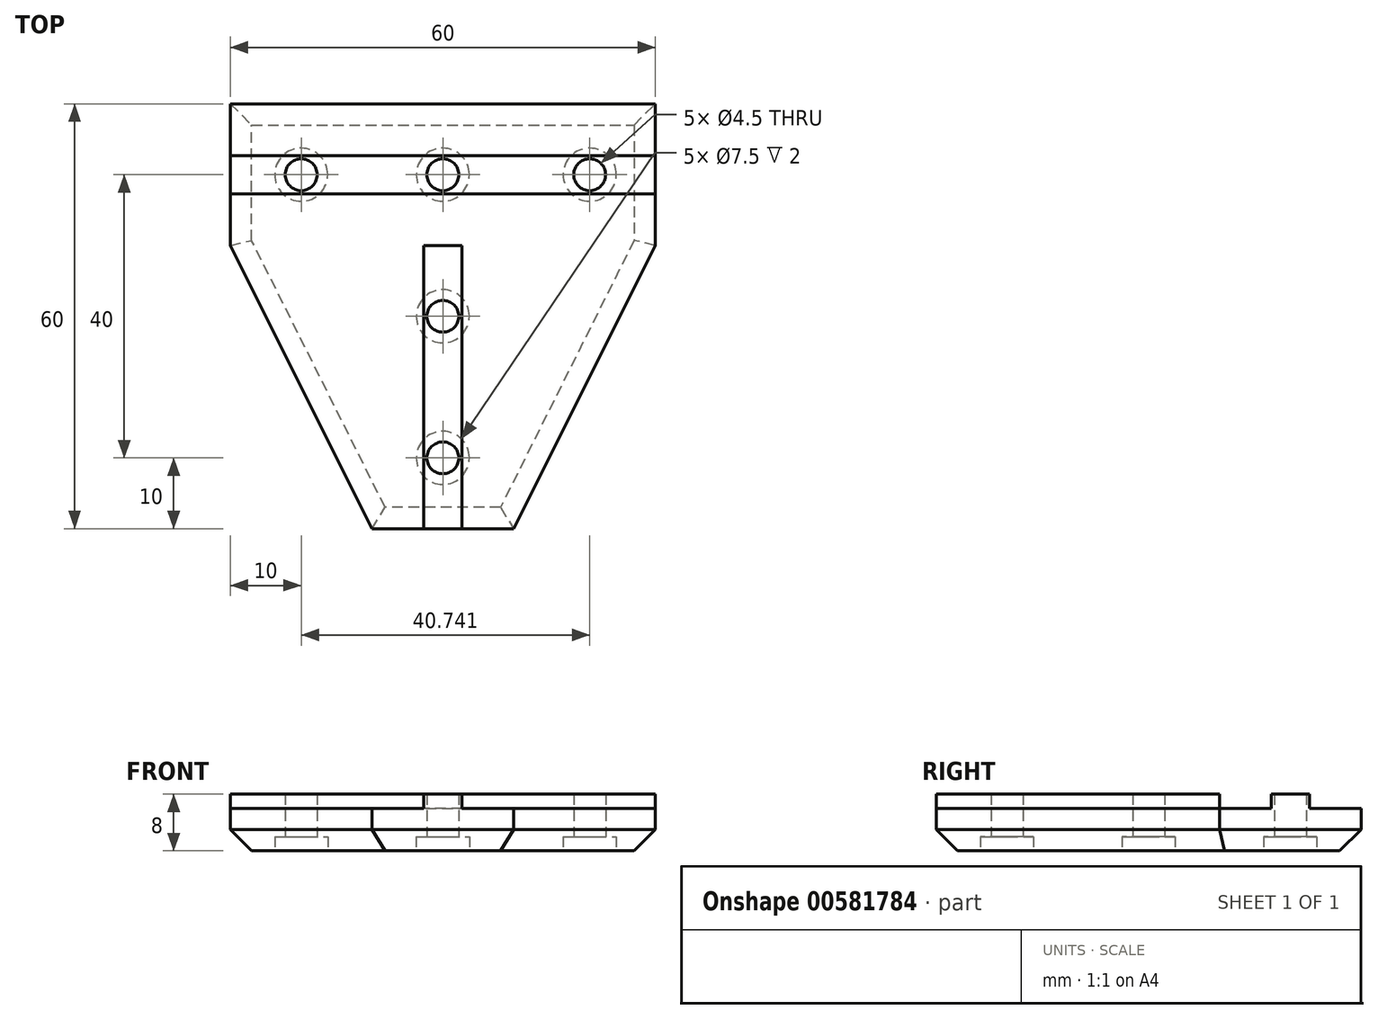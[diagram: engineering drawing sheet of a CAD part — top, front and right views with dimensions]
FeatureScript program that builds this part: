
annotation { "Feature Type Name" : "Feature", "Feature Type Description" : "" }
export const myFeature = defineFeature(function(context is Context, id is Id, definition is map)
    precondition{}
    {
        {
            var Q0;
            Q0=qCreatedBy(makeId("Top.planeOp"),FACE);
            var sketch = newSketch(context, id + "F0", { "sketchPlane" : qUnion([Q0])});
            skLineSegment(sketch, "E0", {"start": v(0, 0) * mm, "end": v(0, 20) * mm, "construction": true});
            skLineSegment(sketch, "E1", {"start": v(0, 0) * mm, "end": v(0, -40) * mm, "construction": true});
            skLineSegment(sketch, "E2", {"start": v(-10, 0) * mm, "end": v(-30, 0) * mm});
            skLineSegment(sketch, "E3", {"start": v(0, 20) * mm, "end": v(-30, 20) * mm});
            skLineSegment(sketch, "E4", {"start": v(-30, 20) * mm, "end": v(-30, 0) * mm});
            skLineSegment(sketch, "E5", {"start": v(0, 20) * mm, "end": v(30, 20) * mm});
            skLineSegment(sketch, "E6", {"start": v(30, 20) * mm, "end": v(30, 0) * mm});
            skLineSegment(sketch, "E7", {"start": v(30, 0) * mm, "end": v(10, 0) * mm});
            skLineSegment(sketch, "E8", {"start": v(0, -40) * mm, "end": v(10, -40) * mm});
            skLineSegment(sketch, "E9", {"start": v(10, -40) * mm, "end": v(10, 0) * mm});
            skLineSegment(sketch, "E10", {"start": v(0, -40) * mm, "end": v(-10, -40) * mm});
            skLineSegment(sketch, "E11", {"start": v(-10, -40) * mm, "end": v(-10, 0) * mm});
            skSolve(sketch);
        }
        {
            var Q0;
            Q0=qSketchRegion(id+"F0",true);
            extrude(context, id + "F1", {"entities" : qUnion([Q0]), "depth" : 6 * mm});
        }
        {
            var Q0;
            Q0=makeQuery(id+"F1.opExtrude","CAP_FACE",FACE,{"disambiguationData":[OSD([sQuery(id+"F0.wireOp",EDGE,"E2"),sQuery(id+"F0.wireOp",EDGE,"E3"),sQuery(id+"F0.wireOp",EDGE,"E4"),sQuery(id+"F0.wireOp",EDGE,"E5"),sQuery(id+"F0.wireOp",EDGE,"E6"),sQuery(id+"F0.wireOp",EDGE,"E7"),sQuery(id+"F0.wireOp",EDGE,"E8"),sQuery(id+"F0.wireOp",EDGE,"E9"),sQuery(id+"F0.wireOp",EDGE,"E10"),sQuery(id+"F0.wireOp",EDGE,"E11")])],"isStart":false});
            var sketch = newSketch(context, id + "F2", { "sketchPlane" : qUnion([Q0])});
            skLineSegment(sketch, "E12", {"start": v(-30, 10) * mm, "end": v(30, 10) * mm, "construction": true});
            skLineSegment(sketch, "E13", {"start": v(0, -40) * mm, "end": v(0, 0) * mm, "construction": true});
            skLineSegment(sketch, "E14", {"start": v(0, 0) * mm, "end": v(-2.71, 0) * mm});
            skLineSegment(sketch, "E15", {"start": v(-2.71, 0) * mm, "end": v(-2.7, -40) * mm});
            skLineSegment(sketch, "E16", {"start": v(2.71, -40) * mm, "end": v(2.71, 0) * mm});
            skLineSegment(sketch, "E17", {"start": v(2.71, 0) * mm, "end": v(0, 0) * mm});
            skLineSegment(sketch, "E18", {"start": v(-2.7, -40) * mm, "end": v(2.71, -40) * mm});
            skLineSegment(sketch, "E19", {"start": v(30, 12.71) * mm, "end": v(30, 7.3) * mm});
            skLineSegment(sketch, "E20", {"start": v(-30, 7.29) * mm, "end": v(30, 7.3) * mm});
            skLineSegment(sketch, "E21", {"start": v(-30, 7.29) * mm, "end": v(-30, 10) * mm});
            skLineSegment(sketch, "E22", {"start": v(-30, 10) * mm, "end": v(-30, 12.71) * mm});
            skLineSegment(sketch, "E23", {"start": v(-30, 12.71) * mm, "end": v(30, 12.71) * mm});
            skSolve(sketch);
        }
        {
            var Q0;
            Q0=qSketchRegion(id+"F2",true);
            extrude(context, id + "F3", {"entities" : qUnion([Q0]), "operationType" : NewBodyOperationType.ADD, "depth" : 2 * mm});
        }
        {
            var Q0;
            Q0=makeQuery(id+"F1.opExtrude","CAP_FACE",FACE,{"disambiguationData":[OSD([sQuery(id+"F0.wireOp",EDGE,"E2"),sQuery(id+"F0.wireOp",EDGE,"E3"),sQuery(id+"F0.wireOp",EDGE,"E4"),sQuery(id+"F0.wireOp",EDGE,"E5"),sQuery(id+"F0.wireOp",EDGE,"E6"),sQuery(id+"F0.wireOp",EDGE,"E7"),sQuery(id+"F0.wireOp",EDGE,"E8"),sQuery(id+"F0.wireOp",EDGE,"E9"),sQuery(id+"F0.wireOp",EDGE,"E10"),sQuery(id+"F0.wireOp",EDGE,"E11")])],"isStart":true});
            var sketch = newSketch(context, id + "F4", { "sketchPlane" : qUnion([Q0])});
            skCircle(sketch, "E24", {"center": v(-20, -10) * mm, "radius": 2.25 * mm});
            skCircle(sketch, "E25", {"center": v(0, 10) * mm, "radius": 2.25 * mm});
            skCircle(sketch, "E26", {"center": v(0, 30) * mm, "radius": 2.25 * mm});
            skCircle(sketch, "E27", {"center": v(20.74, -10) * mm, "radius": 2.25 * mm});
            skCircle(sketch, "E28", {"center": v(0, -10) * mm, "radius": 2.25 * mm});
            skSolve(sketch);
        }
        {
            var Q0;
            Q0=qSketchRegion(id+"F4",true);
            extrude(context, id + "F5", {"entities" : qUnion([Q0]), "operationType" : NewBodyOperationType.REMOVE, "endBound" : BoundingType.THROUGH_ALL, "oppositeDirection" : true, "depth" : 25 * mm});
        }
        {
            var Q0;
            Q0=makeQuery(id+"F1.opExtrude","CAP_FACE",FACE,{"disambiguationData":[OSD([sQuery(id+"F0.wireOp",EDGE,"E2"),sQuery(id+"F0.wireOp",EDGE,"E3"),sQuery(id+"F0.wireOp",EDGE,"E4"),sQuery(id+"F0.wireOp",EDGE,"E5"),sQuery(id+"F0.wireOp",EDGE,"E6"),sQuery(id+"F0.wireOp",EDGE,"E7"),sQuery(id+"F0.wireOp",EDGE,"E8"),sQuery(id+"F0.wireOp",EDGE,"E9"),sQuery(id+"F0.wireOp",EDGE,"E10"),sQuery(id+"F0.wireOp",EDGE,"E11")])],"isStart":true});
            var sketch = newSketch(context, id + "F6", { "sketchPlane" : qUnion([Q0])});
            skCircle(sketch, "E29", {"center": v(0, 30) * mm, "radius": 3.75 * mm});
            skCircle(sketch, "E30", {"center": v(0, 10) * mm, "radius": 3.75 * mm});
            skCircle(sketch, "E31", {"center": v(20.74, -10) * mm, "radius": 3.75 * mm});
            skCircle(sketch, "E32", {"center": v(-20, -10) * mm, "radius": 3.75 * mm});
            skCircle(sketch, "E33", {"center": v(0, -10) * mm, "radius": 3.75 * mm});
            skSolve(sketch);
        }
        {
            var Q0;
            Q0=qSketchRegion(id+"F6",true);
            extrude(context, id + "F7", {"entities" : qUnion([Q0]), "operationType" : NewBodyOperationType.REMOVE, "oppositeDirection" : true, "depth" : 2 * mm});
        }
        {
            var Q0;
            Q0=makeQuery(id+"F1.opExtrude","CAP_FACE",FACE,{"disambiguationData":[OSD([sQuery(id+"F0.wireOp",EDGE,"E2"),sQuery(id+"F0.wireOp",EDGE,"E3"),sQuery(id+"F0.wireOp",EDGE,"E4"),sQuery(id+"F0.wireOp",EDGE,"E5"),sQuery(id+"F0.wireOp",EDGE,"E6"),sQuery(id+"F0.wireOp",EDGE,"E7"),sQuery(id+"F0.wireOp",EDGE,"E8"),sQuery(id+"F0.wireOp",EDGE,"E9"),sQuery(id+"F0.wireOp",EDGE,"E10"),sQuery(id+"F0.wireOp",EDGE,"E11")])],"isStart":true});
            var sketch = newSketch(context, id + "F8", { "sketchPlane" : qUnion([Q0])});
            skLineSegment(sketch, "E34", {"start": v(-10, 40) * mm, "end": v(-30, 0) * mm});
            skLineSegment(sketch, "E35", {"start": v(-30, 0) * mm, "end": v(-10, 0) * mm});
            skLineSegment(sketch, "E36", {"start": v(-10, 0) * mm, "end": v(-10, 40) * mm});
            skLineSegment(sketch, "E37", {"start": v(10, 40) * mm, "end": v(10, 0) * mm});
            skLineSegment(sketch, "E38", {"start": v(10, 0) * mm, "end": v(30, 0) * mm});
            skLineSegment(sketch, "E39", {"start": v(30, 0) * mm, "end": v(10, 40) * mm});
            skSolve(sketch);
        }
        {
            var Q0;
            Q0=qSketchRegion(id+"F8",true);
            extrude(context, id + "F9", {"entities" : qUnion([Q0]), "operationType" : NewBodyOperationType.ADD, "oppositeDirection" : true, "depth" : 6 * mm});
        }
        {
            var Q0;
            Q0=makeQuery(id+"F1.opExtrude","CAP_EDGE",EDGE,{"disambiguationData":[OSD([sQuery(id+"F0.wireOp",EDGE,"E8"),sQuery(id+"F0.wireOp",EDGE,"E10")])],"isStart":true});
            var Q1;
            Q1=makeQuery(id+"F9.opExtrude","CAP_EDGE",EDGE,{"disambiguationData":[OSD([sQuery(id+"F8.wireOp",EDGE,"E34")])],"isStart":true});
            var Q2;
            Q2=makeQuery(id+"F9.opExtrude","CAP_EDGE",EDGE,{"disambiguationData":[OSD([sQuery(id+"F8.wireOp",EDGE,"E39")])],"isStart":true});
            var Q3;
            Q3=makeQuery(id+"F1.opExtrude","CAP_EDGE",EDGE,{"disambiguationData":[OSD([sQuery(id+"F0.wireOp",EDGE,"E6")])],"isStart":true});
            var Q4;
            Q4=makeQuery(id+"F1.opExtrude","CAP_EDGE",EDGE,{"disambiguationData":[OSD([sQuery(id+"F0.wireOp",EDGE,"E3"),sQuery(id+"F0.wireOp",EDGE,"E5")])],"isStart":true});
            var Q5;
            Q5=makeQuery(id+"F1.opExtrude","CAP_EDGE",EDGE,{"disambiguationData":[OSD([sQuery(id+"F0.wireOp",EDGE,"E4")])],"isStart":true});
            chamfer(context, id + "F10", {"entities" : qUnion([Q0, Q1, Q2, Q3, Q4, Q5]), "width" : 3 * mm, "tangentPropagation" : true});
        }
    });
